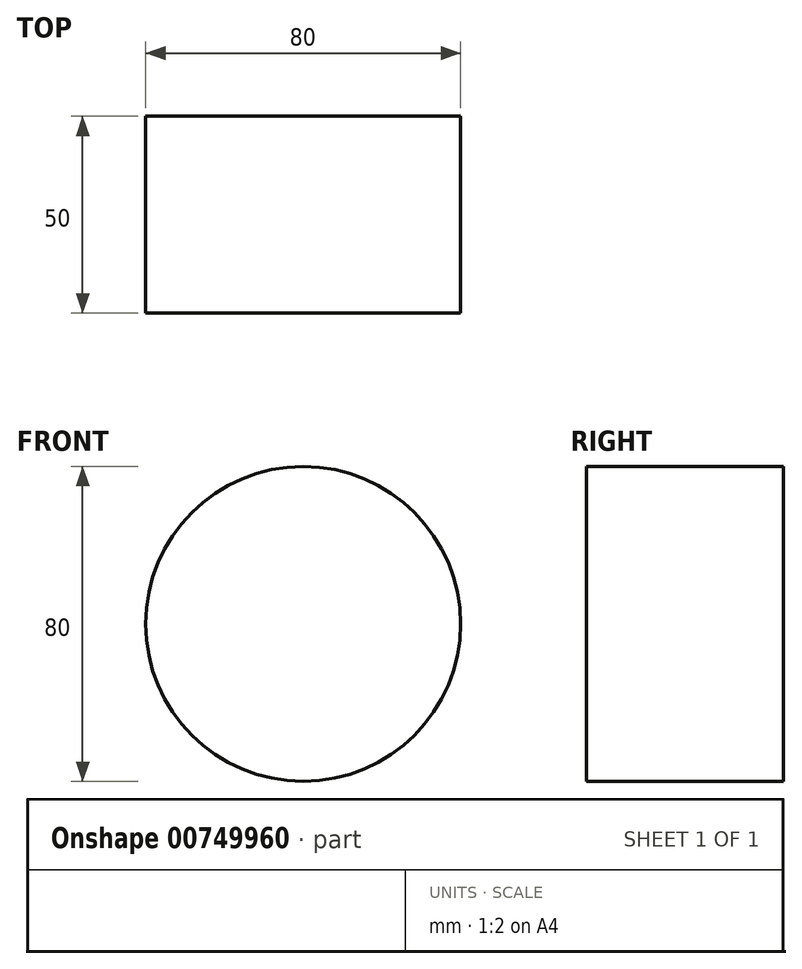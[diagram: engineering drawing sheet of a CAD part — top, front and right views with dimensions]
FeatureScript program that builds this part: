
annotation { "Feature Type Name" : "Feature", "Feature Type Description" : "" }
export const myFeature = defineFeature(function(context is Context, id is Id, definition is map)
    precondition{}
    {
        {
            var Q0;
            Q0=qCreatedBy(makeId("Front.planeOp"),FACE);
            var sketch = newSketch(context, id + "F0", { "sketchPlane" : qUnion([Q0])});
            skCircle(sketch, "E0", {"center": v(0, 0) * mm, "radius": 40 * mm});
            skSolve(sketch);
        }
        {
            var Q0;
            Q0=makeQuery(id+"F0.imprint","IMPRINT",FACE,{"disambiguationData":[TD([[makeQuery(id+"F0.imprint","IMPRINT",EDGE,{"derivedFrom":sQuery(id+"F0.wireOp",EDGE,"E0")}),1.0]])]});
            extrude(context, id + "F1", {"entities" : qUnion([Q0]), "depth" : 50 * mm, "offsetDistance" : 25 * mm});
        }
    });
